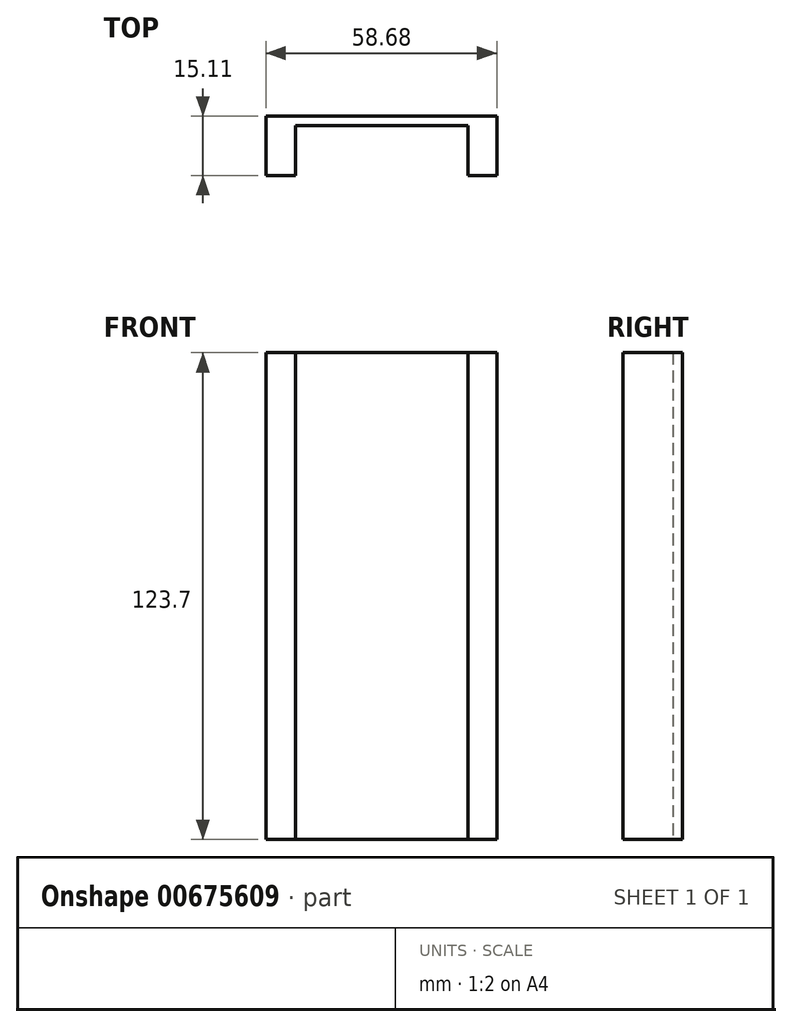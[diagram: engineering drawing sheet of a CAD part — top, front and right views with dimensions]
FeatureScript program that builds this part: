
annotation { "Feature Type Name" : "Feature", "Feature Type Description" : "" }
export const myFeature = defineFeature(function(context is Context, id is Id, definition is map)
    precondition{}
    {
        {
            var Q0;
            Q0=qCreatedBy(makeId("Front.planeOp"),FACE);
            var sketch = newSketch(context, id + "F0", { "sketchPlane" : qUnion([Q0])});
            skLineSegment(sketch, "E0.bottom", {"start": v(-29.34, 61.85) * mm, "end": v(29.34, 61.85) * mm});
            skLineSegment(sketch, "E0.top", {"start": v(-29.34, -61.85) * mm, "end": v(29.34, -61.85) * mm});
            skLineSegment(sketch, "E0.left", {"start": v(-29.34, 61.85) * mm, "end": v(-29.34, -61.85) * mm});
            skLineSegment(sketch, "E0.right", {"start": v(29.34, 61.85) * mm, "end": v(29.34, -61.85) * mm});
            skPoint(sketch, "E0.middle", {"position": v(0, 0) * mm});
            skSolve(sketch);
        }
        {
            var Q0;
            Q0=makeQuery(id+"F0.imprint","IMPRINT",FACE,{"disambiguationData":[TD([[makeQuery(id+"F0.imprint","IMPRINT",EDGE,{"derivedFrom":sQuery(id+"F0.wireOp",EDGE,"E0.bottom")}),-1.0]])]});
            extrude(context, id + "F1", {"entities" : qUnion([Q0]), "depth" : 2.41 * mm, "offsetDistance" : 25.4 * mm});
        }
        {
            var Q0;
            Q0=makeQuery(id+"F1.opExtrude","CAP_FACE",FACE,{"disambiguationData":[OSD([sQuery(id+"F0.wireOp",EDGE,"E0.bottom"),sQuery(id+"F0.wireOp",EDGE,"E0.top"),sQuery(id+"F0.wireOp",EDGE,"E0.left"),sQuery(id+"F0.wireOp",EDGE,"E0.right")])],"isStart":false});
            var sketch = newSketch(context, id + "F2", { "sketchPlane" : qUnion([Q0])});
            skLineSegment(sketch, "E1.bottom", {"start": v(-29.34, 61.85) * mm, "end": v(-21.75, 61.85) * mm});
            skLineSegment(sketch, "E1.top", {"start": v(-29.34, -61.85) * mm, "end": v(-21.75, -61.85) * mm});
            skLineSegment(sketch, "E1.left", {"start": v(-29.34, 61.85) * mm, "end": v(-29.34, -61.85) * mm});
            skLineSegment(sketch, "E1.right", {"start": v(-21.75, 61.85) * mm, "end": v(-21.75, -61.85) * mm});
            skLineSegment(sketch, "E2.bottom", {"start": v(29.34, 61.85) * mm, "end": v(22.05, 61.85) * mm});
            skLineSegment(sketch, "E2.top", {"start": v(29.34, -61.85) * mm, "end": v(22.05, -61.85) * mm});
            skLineSegment(sketch, "E2.left", {"start": v(29.34, 61.85) * mm, "end": v(29.34, -61.85) * mm});
            skLineSegment(sketch, "E2.right", {"start": v(22.05, 61.85) * mm, "end": v(22.05, -61.85) * mm});
            skSolve(sketch);
        }
        {
            var Q0;
            Q0 = qSketchRegion(id + "F2", true);
            extrude(context, id + "F3", {"entities" : qUnion([Q0]), "operationType" : NewBodyOperationType.ADD, "depth" : 12.7 * mm, "offsetDistance" : 25.4 * mm});
        }
    });
